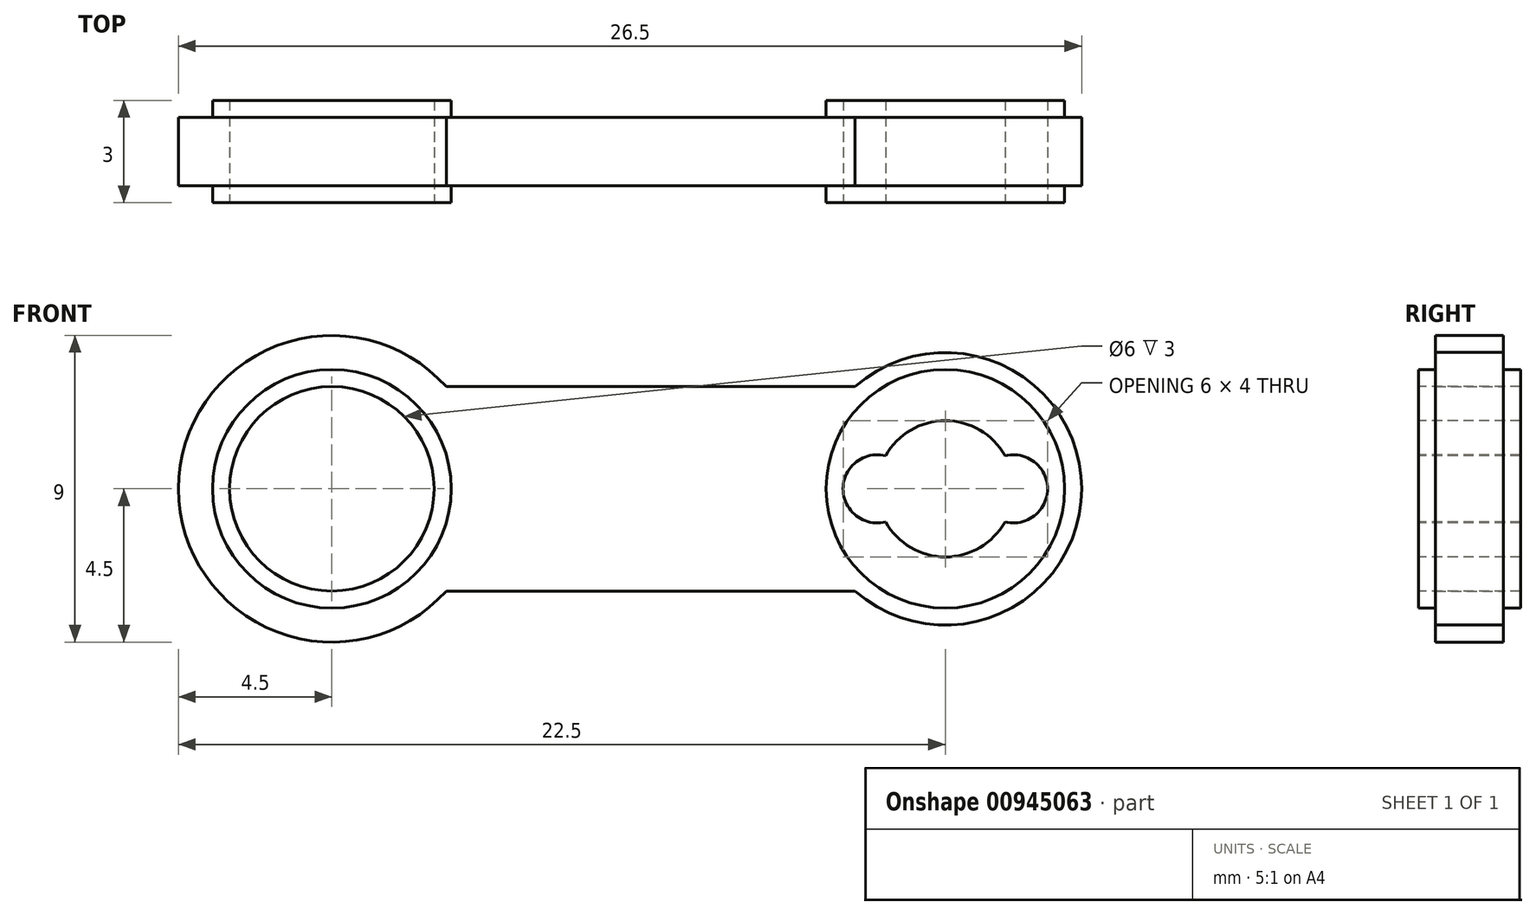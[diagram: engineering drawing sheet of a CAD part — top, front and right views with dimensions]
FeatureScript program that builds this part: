
annotation { "Feature Type Name" : "Feature", "Feature Type Description" : "" }
export const myFeature = defineFeature(function(context is Context, id is Id, definition is map)
    precondition{}
    {
        {
            var Q0;
            Q0=qCreatedBy(makeId("Front.planeOp"),FACE);
            var sketch = newSketch(context, id + "F0", { "sketchPlane" : qUnion([Q0])});
            skArc(sketch, "E0", {"start": v(3.35, 3) * mm, "mid": v(-4.5, 0) * mm, "end": v(3.35, -3) * mm});
            skArc(sketch, "E1", {"start": v(15.35, -3) * mm, "mid": v(22, 0) * mm, "end": v(15.35, 3) * mm});
            skLineSegment(sketch, "E2", {"start": v(3.35, 3) * mm, "end": v(15.35, 3) * mm});
            skLineSegment(sketch, "E3", {"start": v(3.35, -3) * mm, "end": v(15.35, -3) * mm});
            skSolve(sketch);
        }
        {
            var Q0;
            Q0=makeQuery(id+"F0.imprint","IMPRINT",FACE,{"disambiguationData":[TD([[makeQuery(id+"F0.imprint","IMPRINT",EDGE,{"derivedFrom":sQuery(id+"F0.wireOp",EDGE,"E0")}),1.0]])]});
            extrude(context, id + "F1", {"entities" : qUnion([Q0]), "depth" : 2 * mm, "offsetDistance" : 25 * mm, "symmetric" : true});
        }
        {
            var Q0;
            Q0=qCreatedBy(makeId("Front.planeOp"),FACE);
            var sketch = newSketch(context, id + "F2", { "sketchPlane" : qUnion([Q0])});
            skCircle(sketch, "E4", {"center": v(0, 0) * mm, "radius": 3.5 * mm});
            skCircle(sketch, "E5", {"center": v(18, 0) * mm, "radius": 3.5 * mm});
            skSolve(sketch);
        }
        {
            var Q0;
            Q0 = qSketchRegion(id + "F2", true);
            extrude(context, id + "F3", {"entities" : qUnion([Q0]), "operationType" : NewBodyOperationType.ADD, "depth" : 3 * mm, "offsetDistance" : 25 * mm, "symmetric" : true});
        }
        {
            var Q0;
            Q0=makeQuery(id+"F3.opExtrude","CAP_FACE",FACE,{"disambiguationData":[OSD([sQuery(id+"F2.wireOp",EDGE,"E4")])],"isStart":false});
            var sketch = newSketch(context, id + "F4", { "sketchPlane" : qUnion([Q0])});
            skCircle(sketch, "E6", {"center": v(0, 0) * mm, "radius": 3 * mm});
            skArc(sketch, "E7", {"start": v(19.75, 0.97) * mm, "mid": v(18, 2) * mm, "end": v(16.25, 0.97) * mm});
            skArc(sketch, "E8", {"start": v(16.25, 0.97) * mm, "mid": v(15, 0) * mm, "end": v(16.25, -0.97) * mm});
            skArc(sketch, "E9", {"start": v(19.75, -0.97) * mm, "mid": v(21, 0) * mm, "end": v(19.75, 0.97) * mm});
            skArc(sketch, "E10.trimOffspring", {"start": v(16.25, -0.97) * mm, "mid": v(18, -2) * mm, "end": v(19.75, -0.97) * mm});
            skSolve(sketch);
        }
        {
            var Q0;
            Q0=makeQuery(id+"F4.imprint","IMPRINT",FACE,{"disambiguationData":[TD([[makeQuery(id+"F4.imprint","IMPRINT",EDGE,{"derivedFrom":sQuery(id+"F4.wireOp",EDGE,"E6")}),1.0]])]});
            var Q1;
            Q1=makeQuery(id+"F4.imprint","IMPRINT",FACE,{"disambiguationData":[TD([[makeQuery(id+"F4.imprint","IMPRINT",EDGE,{"derivedFrom":sQuery(id+"F4.wireOp",EDGE,"E7")}),1.0]])]});
            extrude(context, id + "F5", {"entities" : qUnion([Q0, Q1]), "operationType" : NewBodyOperationType.REMOVE, "endBound" : BoundingType.THROUGH_ALL, "oppositeDirection" : true, "depth" : 25 * mm, "offsetDistance" : 25 * mm});
        }
    });
